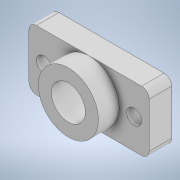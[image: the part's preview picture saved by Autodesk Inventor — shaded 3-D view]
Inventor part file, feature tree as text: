
AUTODESK INVENTOR PART (.ipt)
format: ipt  version: 2020.2 (Build 242310000, 310)  size: 142,848 bytes
history: native  units: mm
features: extrude x2, sketch x2, fillet x1
ambient origin geometry x8: Origin, YZ Plane, XZ Plane, XY Plane, X Axis, Y Axis, Z Axis, Center Point
bodies: Solid1 (feature_tree)
feature tree (5):
  extrude  "Extrusion1"  Depth=8.0mm
  extrude  "Extrusion2"  Depth=1.0mm
  fillet  "Fillet1"  Radius=2.0mm
  sketch  "Sketch1"  dims[d0=8.0mm d1=4.52mm]
  sketch  "Sketch2"  dims[d2=5.75mm d3=0.0mm d7=2.0mm d8=2.0mm d9=6.0mm d10=6.0mm d11=0.0mm d12=0.0mm d13=3.0mm d14=0.0mm d19=16.0mm d20=8.0mm d21=1.0mm d29=9.599311mm d47=9.599311mm d65=9.599311mm]
